# Revit family: DISS - Wall Compatible Outlet
name_source: partatom
category: Generic Models
revit_build: Autodesk Revit 2018 (Build: 20180423_1000(x64)
units: mm (PartAtom-declared; Revit-internal decimal feet)

## family parameters
Can host rebar = No
Cut with Voids When Loaded = No
Host = Face
Part Type = Normal
Room Calculation Point = No
Round Connector Dimension = Use Diameter
Shared = Yes

## types (3) — shared parameters
Default Elevation = 1219.2 mm  [stored 4 ft]
Description = Amico Alert-1 Series Outlet
Face Plate = Amico_Stainless_Steel [Wall Outlet]
GWB (Thickness) = 16 mm  [stored 0.0524934 ft]
Outlet = Amico_Stainless Steel, Polished
Pipe = Copper
Pipe Length = 200 mm
URL = http://www.amico.com

## per-type parameters (varying)
| type | Air Type | Manufacturer | MedVac | Model | Oxygen | Pipe I.D. | Pipe O.D. |
| Medical Air | DISS MedAir [Wall Outlet] | Amico | No | O-DISWAL-U-AIR | No | 13.375 mm  [stored 0.0438812 ft] | 15.875 mm |
| Oxygen | DISS Oxygen [Wall Outlet] | Amico Pipeline | No | O-DISWAL-U-OXY | Yes | 13.375 mm  [stored 0.0438812 ft] | 15.875 mm |
| MedVac | DISS Vac [Wall Outlet] | Amico | Yes | O-DISWAL-U-VAC | No | 19.725 mm | 22.225 mm |

type visibility flags (boolean, named after types; folded from table):
- Medical Air: Yes: Medical Air
- Oxygen: Yes: (none)
- MedVac: Yes: (none)

note: [stored X ft] marks values corroborated as IEEE doubles in the binary element streams (Revit-internal decimal feet)

## geometry (parser evidence)
native form markers: Sweep x6
no freeform markers — native parametric forms only
